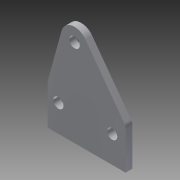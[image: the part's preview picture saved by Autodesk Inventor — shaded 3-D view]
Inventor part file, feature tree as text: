
AUTODESK INVENTOR PART (.ipt)
format: ipt  version: 2014 (Build 180170000, 170)  size: 101,888 bytes
history: native  units: in
note: dims shown in document units (in); Inventor stores cm internally (conversion verified against a paired STEP export)
features: extrude x1, fillet x1, sketch x1
ambient origin geometry x8: Origin, YZ Plane, XZ Plane, XY Plane, X Axis, Y Axis, Z Axis, Center Point
bodies: Solid1 (feature_tree)
feature tree (3):
  extrude  "Extrusion1"  Depth=0.125in TaperAngle=0.0deg
  fillet  "Fillet1"  Radius=0.5in
  sketch  "Sketch1"  dims[d1=0.19in d3=0.125in d4=0.0in d5=0.5in d6=0.25in d7=0.2in d9=0.25in d10=1.0in d14=0.5in d15=0.75in d16=0.194in d17=0.25in d18=0.125in]
